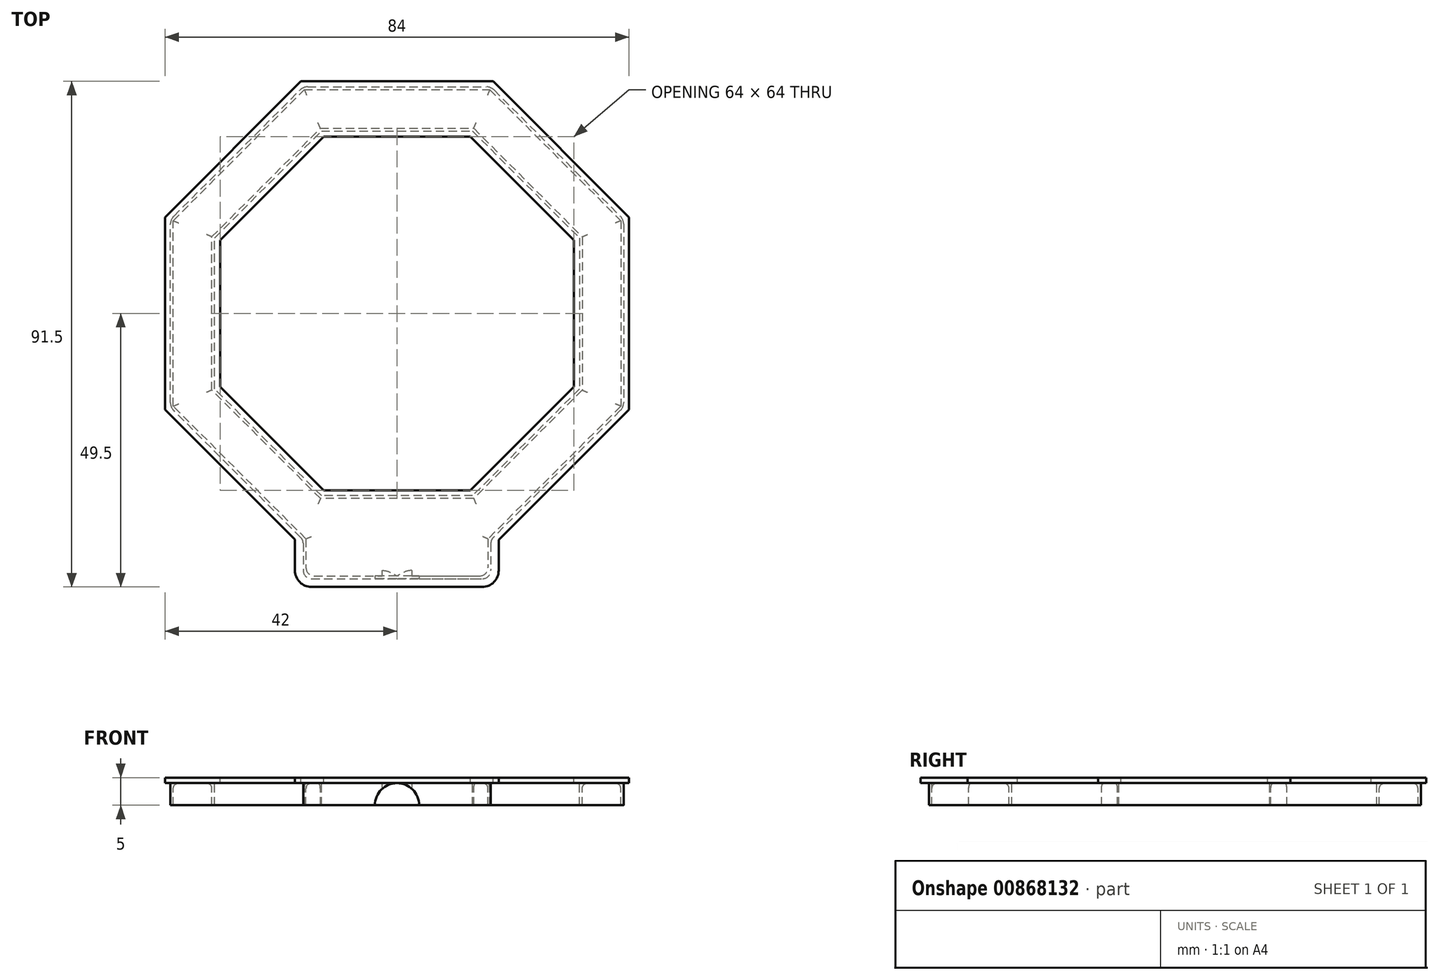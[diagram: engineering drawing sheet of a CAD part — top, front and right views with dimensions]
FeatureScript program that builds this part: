
annotation { "Feature Type Name" : "Feature", "Feature Type Description" : "" }
export const myFeature = defineFeature(function(context is Context, id is Id, definition is map)
    precondition{}
    {
        {
            var Q0;
            Q0=qCreatedBy(makeId("Top.planeOp"),FACE);
            var sketch = newSketch(context, id + "F0", { "sketchPlane" : qUnion([Q0])});
            skCircle(sketch, "E0.cCircle", {"center": v(0, 0) * mm, "radius": 41 * mm, "construction": true});
            skLineSegment(sketch, "E0.0", {"start": v(41, 16.98) * mm, "end": v(41, -16.98) * mm});
            skLineSegment(sketch, "E0.1", {"start": v(41, -16.98) * mm, "end": v(16.98, -41) * mm});
            skLineSegment(sketch, "E0.3", {"start": v(-16.98, -41) * mm, "end": v(-41, -16.98) * mm});
            skLineSegment(sketch, "E0.4", {"start": v(-41, -16.98) * mm, "end": v(-41, 16.98) * mm});
            skLineSegment(sketch, "E0.5", {"start": v(-41, 16.98) * mm, "end": v(-16.98, 41) * mm});
            skLineSegment(sketch, "E0.6", {"start": v(-16.98, 41) * mm, "end": v(16.98, 41) * mm});
            skLineSegment(sketch, "E0.7", {"start": v(16.98, 41) * mm, "end": v(41, 16.98) * mm});
            skPoint(sketch, "E0.0.midPoint", {"position": v(41, 0) * mm});
            skCircle(sketch, "E1.cCircle", {"center": v(0, 0) * mm, "radius": 33 * mm, "construction": true});
            skLineSegment(sketch, "E1.0", {"start": v(-33, 13.67) * mm, "end": v(-13.67, 33) * mm});
            skLineSegment(sketch, "E1.1", {"start": v(-13.67, 33) * mm, "end": v(13.67, 33) * mm});
            skLineSegment(sketch, "E1.2", {"start": v(13.67, 33) * mm, "end": v(33, 13.67) * mm});
            skLineSegment(sketch, "E1.3", {"start": v(33, 13.67) * mm, "end": v(33, -13.67) * mm});
            skLineSegment(sketch, "E1.4", {"start": v(33, -13.67) * mm, "end": v(13.67, -33) * mm});
            skLineSegment(sketch, "E1.5", {"start": v(13.67, -33) * mm, "end": v(-13.67, -33) * mm});
            skLineSegment(sketch, "E1.6", {"start": v(-13.67, -33) * mm, "end": v(-33, -13.67) * mm});
            skLineSegment(sketch, "E1.7", {"start": v(-33, -13.67) * mm, "end": v(-33, 13.67) * mm});
            skPoint(sketch, "E1.0.midPoint", {"position": v(-23.33, 23.33) * mm});
            skLineSegment(sketch, "E2.left", {"start": v(-16.98, -41) * mm, "end": v(-16.98, -48) * mm});
            skCircle(sketch, "E3.cCircle", {"center": v(0, 0) * mm, "radius": 32 * mm, "construction": true});
            skLineSegment(sketch, "E3.0", {"start": v(-13.25, 32) * mm, "end": v(13.25, 32) * mm});
            skLineSegment(sketch, "E3.1", {"start": v(13.25, 32) * mm, "end": v(32, 13.25) * mm});
            skLineSegment(sketch, "E3.2", {"start": v(32, 13.25) * mm, "end": v(32, -13.25) * mm});
            skLineSegment(sketch, "E3.3", {"start": v(32, -13.25) * mm, "end": v(13.25, -32) * mm});
            skLineSegment(sketch, "E3.4", {"start": v(13.25, -32) * mm, "end": v(-13.25, -32) * mm});
            skLineSegment(sketch, "E3.5", {"start": v(-13.25, -32) * mm, "end": v(-32, -13.25) * mm});
            skLineSegment(sketch, "E3.6", {"start": v(-32, -13.25) * mm, "end": v(-32, 13.25) * mm});
            skLineSegment(sketch, "E3.7", {"start": v(-32, 13.25) * mm, "end": v(-13.25, 32) * mm});
            skPoint(sketch, "E3.0.midPoint", {"position": v(0, 32) * mm});
            skCircle(sketch, "E4.cCircle", {"center": v(0, 0) * mm, "radius": 42 * mm, "construction": true});
            skLineSegment(sketch, "E4.0", {"start": v(-42, 17.4) * mm, "end": v(-17.4, 42) * mm});
            skLineSegment(sketch, "E4.1", {"start": v(-17.4, 42) * mm, "end": v(17.4, 42) * mm});
            skLineSegment(sketch, "E4.2", {"start": v(17.4, 42) * mm, "end": v(42, 17.4) * mm});
            skLineSegment(sketch, "E4.3", {"start": v(42, 17.4) * mm, "end": v(42, -17.4) * mm});
            skLineSegment(sketch, "E4.4", {"start": v(42, -17.4) * mm, "end": v(18.4, -41) * mm});
            skLineSegment(sketch, "E4.6", {"start": v(-18.48, -40.91) * mm, "end": v(-42, -17.4) * mm});
            skLineSegment(sketch, "E4.7", {"start": v(-42, -17.4) * mm, "end": v(-42, 17.4) * mm});
            skPoint(sketch, "E4.0.midPoint", {"position": v(-29.7, 29.7) * mm});
            skLineSegment(sketch, "E5", {"start": v(-18.48, -40.91) * mm, "end": v(-18.48, -49.5) * mm});
            skPoint(sketch, "E6.orphan", {"position": v(-17.4, -42) * mm});
            skLineSegment(sketch, "E7", {"start": v(-16.98, -48) * mm, "end": v(16.98, -48) * mm});
            skLineSegment(sketch, "E8", {"start": v(-18.48, -49.5) * mm, "end": v(18.4, -49.5) * mm});
            skLineSegment(sketch, "E9", {"start": v(18.4, -49.5) * mm, "end": v(18.4, -41) * mm});
            skLineSegment(sketch, "E10", {"start": v(16.98, -41) * mm, "end": v(16.98, -48) * mm});
            skLineSegment(sketch, "E11.0", {"start": v(-33.5, 13.88) * mm, "end": v(-13.88, 33.5) * mm});
            skLineSegment(sketch, "E11.1", {"start": v(-33.5, -13.88) * mm, "end": v(-33.5, 13.88) * mm});
            skLineSegment(sketch, "E11.2", {"start": v(-13.88, 33.5) * mm, "end": v(13.88, 33.5) * mm});
            skLineSegment(sketch, "E11.3", {"start": v(-13.88, -33.5) * mm, "end": v(-33.5, -13.88) * mm});
            skLineSegment(sketch, "E11.4", {"start": v(13.88, 33.5) * mm, "end": v(33.5, 13.88) * mm});
            skLineSegment(sketch, "E11.5", {"start": v(33.5, 13.88) * mm, "end": v(33.5, -13.88) * mm});
            skLineSegment(sketch, "E11.6", {"start": v(33.5, -13.88) * mm, "end": v(13.88, -33.5) * mm});
            skLineSegment(sketch, "E11.7", {"start": v(13.88, -33.5) * mm, "end": v(-13.88, -33.5) * mm});
            skLineSegment(sketch, "E12.0", {"start": v(-16.48, -40.8) * mm, "end": v(-16.48, -47.5) * mm});
            skLineSegment(sketch, "E12.1", {"start": v(-16.48, -47.5) * mm, "end": v(16.48, -47.5) * mm});
            skLineSegment(sketch, "E12.2", {"start": v(-16.48, -40.8) * mm, "end": v(-40.5, -16.78) * mm});
            skLineSegment(sketch, "E12.3", {"start": v(16.48, -40.8) * mm, "end": v(16.48, -47.5) * mm});
            skLineSegment(sketch, "E12.4", {"start": v(40.5, -16.78) * mm, "end": v(16.48, -40.8) * mm});
            skLineSegment(sketch, "E12.5", {"start": v(40.5, 16.78) * mm, "end": v(40.5, -16.78) * mm});
            skLineSegment(sketch, "E12.6", {"start": v(-40.5, -16.78) * mm, "end": v(-40.5, 16.78) * mm});
            skLineSegment(sketch, "E12.7", {"start": v(-40.5, 16.78) * mm, "end": v(-16.78, 40.5) * mm});
            skLineSegment(sketch, "E12.8", {"start": v(-16.78, 40.5) * mm, "end": v(16.78, 40.5) * mm});
            skLineSegment(sketch, "E12.9", {"start": v(16.78, 40.5) * mm, "end": v(40.5, 16.78) * mm});
            skSolve(sketch);
        }
        {
            var Q0;
            Q0=makeQuery(id+"F0.imprint","IMPRINT",FACE,{"disambiguationData":[TD([[makeQuery(id+"F0.imprint","IMPRINT",EDGE,{"derivedFrom":sQuery(id+"F0.wireOp",EDGE,"E1.0")}),1.0]])]});
            var Q1;
            Q1=makeQuery(id+"F0.imprint","IMPRINT",FACE,{"disambiguationData":[TD([[makeQuery(id+"F0.imprint","IMPRINT",EDGE,{"derivedFrom":sQuery(id+"F0.wireOp",EDGE,"E0.0")}),-1.0]])]});
            extrude(context, id + "F1", {"entities" : qUnion([Q0, Q1]), "oppositeDirection" : true, "depth" : 5 * mm, "offsetDistance" : 25 * mm});
        }
        {
            var Q0;
            Q0=makeQuery(id+"F0.imprint","IMPRINT",FACE,{"disambiguationData":[TD([[makeQuery(id+"F0.imprint","IMPRINT",EDGE,{"derivedFrom":sQuery(id+"F0.wireOp",EDGE,"E1.0")}),-1.0]])]});
            var Q1;
            Q1=makeQuery(id+"F0.imprint","IMPRINT",FACE,{"disambiguationData":[TD([[makeQuery(id+"F0.imprint","IMPRINT",EDGE,{"derivedFrom":sQuery(id+"F0.wireOp",EDGE,"E11.0")}),1.0]])]});
            var Q2;
            Q2=makeQuery(id+"F0.imprint","IMPRINT",FACE,{"disambiguationData":[TD([[makeQuery(id+"F0.imprint","IMPRINT",EDGE,{"derivedFrom":sQuery(id+"F0.wireOp",EDGE,"E0.0")}),1.0]])]});
            extrude(context, id + "F2", {"entities" : qUnion([Q0, Q1, Q2]), "operationType" : NewBodyOperationType.ADD, "oppositeDirection" : true, "depth" : 1 * mm, "offsetDistance" : 25 * mm});
        }
        {
            var Q0;
            Q0=makeQuery(id+"F1.opExtrude","SWEPT_FACE",FACE,{"disambiguationData":[OSD([sQuery(id+"F0.wireOp",EDGE,"E7")])]});
            var sketch = newSketch(context, id + "F3", { "sketchPlane" : qUnion([Q0])});
            skCircle(sketch, "E13", {"center": v(0, -5) * mm, "radius": 4 * mm});
            skSolve(sketch);
        }
        {
            var Q0;
            {var subQ0=sQuery(id+"F3.wireOp",EDGE,"E13");var subQ1=sQuery(id+"F0.wireOp",EDGE,"E7");var subQ2=makeQuery(id+"F3.imprint","INTERSECT",VERTEX,{"derivedFrom":[makeQuery(id+"F2.opExtrude","CAP_EDGE",EDGE,{"disambiguationData":[OSD([subQ1])],"isStart":false}),subQ0]});Q0=makeQuery(id+"F3.imprint","IMPRINT",FACE,{"disambiguationData":[TD([[makeQuery(id+"F3.imprint","IMPRINT",EDGE,{"disambiguationData":[TD([[subQ2,1.0]])],"derivedFrom":subQ0}),1.0]])]});}
            extrude(context, id + "F4", {"entities" : qUnion([Q0]), "operationType" : NewBodyOperationType.REMOVE, "oppositeDirection" : true, "depth" : 3 * mm, "offsetDistance" : 25 * mm});
        }
        {
            var Q0;
            Q0=makeQuery(id+"F1.opExtrude","SWEPT_EDGE",EDGE,{"disambiguationData":[OSD([sQuery(id+"F0.wireOp",EDGE,"E0.0"),sQuery(id+"F0.wireOp",EDGE,"E0.7")])]});
            var Q1;
            Q1=makeQuery(id+"F1.opExtrude","SWEPT_EDGE",EDGE,{"disambiguationData":[OSD([sQuery(id+"F0.wireOp",EDGE,"E0.0"),sQuery(id+"F0.wireOp",EDGE,"E0.1")])]});
            var Q2;
            Q2=makeQuery(id+"F1.opExtrude","SWEPT_EDGE",EDGE,{"disambiguationData":[OSD([sQuery(id+"F0.wireOp",EDGE,"E0.3"),sQuery(id+"F0.wireOp",EDGE,"E0.4")])]});
            var Q3;
            Q3=makeQuery(id+"F1.opExtrude","SWEPT_EDGE",EDGE,{"disambiguationData":[OSD([sQuery(id+"F0.wireOp",EDGE,"E0.4"),sQuery(id+"F0.wireOp",EDGE,"E0.5")])]});
            var Q4;
            Q4=makeQuery(id+"F1.opExtrude","SWEPT_EDGE",EDGE,{"disambiguationData":[OSD([sQuery(id+"F0.wireOp",EDGE,"E0.5"),sQuery(id+"F0.wireOp",EDGE,"E0.6")])]});
            var Q5;
            Q5=makeQuery(id+"F1.opExtrude","SWEPT_EDGE",EDGE,{"disambiguationData":[OSD([sQuery(id+"F0.wireOp",EDGE,"E0.6"),sQuery(id+"F0.wireOp",EDGE,"E0.7")])]});
            fillet(context, id + "F5", {"entities" : qUnion([Q0, Q1, Q2, Q3, Q4, Q5]), "radius" : 2 * mm, "tangentPropagation" : true, "allowEdgeOverflow" : false});
        }
        {
            var Q0;
            Q0=makeQuery(id+"F1.opExtrude","SWEPT_EDGE",EDGE,{"disambiguationData":[OSD([sQuery(id+"F0.wireOp",EDGE,"E0.1"),sQuery(id+"F0.wireOp",EDGE,"E10")])]});
            var Q1;
            Q1=makeQuery(id+"F1.opExtrude","SWEPT_EDGE",EDGE,{"disambiguationData":[OSD([sQuery(id+"F0.wireOp",EDGE,"E0.3"),sQuery(id+"F0.wireOp",EDGE,"E2.left")])]});
            var Q2;
            Q2=makeQuery(id+"F1.opExtrude","SWEPT_EDGE",EDGE,{"disambiguationData":[OSD([sQuery(id+"F0.wireOp",EDGE,"E7"),sQuery(id+"F0.wireOp",EDGE,"E10")])]});
            var Q3;
            Q3=makeQuery(id+"F1.opExtrude","SWEPT_EDGE",EDGE,{"disambiguationData":[OSD([sQuery(id+"F0.wireOp",EDGE,"E12.0"),sQuery(id+"F0.wireOp",EDGE,"E12.1")])]});
            var Q4;
            Q4=makeQuery(id+"F1.opExtrude","SWEPT_EDGE",EDGE,{"disambiguationData":[OSD([sQuery(id+"F0.wireOp",EDGE,"E12.1"),sQuery(id+"F0.wireOp",EDGE,"E12.3")])]});
            var Q5;
            Q5=makeQuery(id+"F1.opExtrude","SWEPT_EDGE",EDGE,{"disambiguationData":[OSD([sQuery(id+"F0.wireOp",EDGE,"E2.left"),sQuery(id+"F0.wireOp",EDGE,"E7")])]});
            fillet(context, id + "F6", {"entities" : qUnion([Q0, Q1, Q2, Q3, Q4, Q5]), "radius" : 1.5 * mm, "tangentPropagation" : true, "allowEdgeOverflow" : false});
        }
        {
            var Q0;
            Q0=makeQuery(id+"F2.opExtrude","CAP_FACE",FACE,{"disambiguationData":[OSD([sQuery(id+"F0.wireOp",EDGE,"E11.0"),sQuery(id+"F0.wireOp",EDGE,"E11.1"),sQuery(id+"F0.wireOp",EDGE,"E11.2"),sQuery(id+"F0.wireOp",EDGE,"E11.3"),sQuery(id+"F0.wireOp",EDGE,"E11.4"),sQuery(id+"F0.wireOp",EDGE,"E11.5"),sQuery(id+"F0.wireOp",EDGE,"E11.6"),sQuery(id+"F0.wireOp",EDGE,"E11.7"),sQuery(id+"F0.wireOp",EDGE,"E12.0"),sQuery(id+"F0.wireOp",EDGE,"E12.1"),sQuery(id+"F0.wireOp",EDGE,"E12.2"),sQuery(id+"F0.wireOp",EDGE,"E12.3"),sQuery(id+"F0.wireOp",EDGE,"E12.4"),sQuery(id+"F0.wireOp",EDGE,"E12.5"),sQuery(id+"F0.wireOp",EDGE,"E12.6"),sQuery(id+"F0.wireOp",EDGE,"E12.7"),sQuery(id+"F0.wireOp",EDGE,"E12.8"),sQuery(id+"F0.wireOp",EDGE,"E12.9")])],"isStart":false});
            fillet(context, id + "F7", {"entities" : qUnion([Q0]), "radius" : 1 * mm, "tangentPropagation" : true, "allowEdgeOverflow" : false});
        }
        {
            var Q0;
            Q0=makeQuery(id+"F2.opExtrude","SWEPT_EDGE",EDGE,{"disambiguationData":[OSD([sQuery(id+"F0.wireOp",EDGE,"E8"),sQuery(id+"F0.wireOp",EDGE,"E9")])]});
            var Q1;
            Q1=makeQuery(id+"F2.opExtrude","SWEPT_EDGE",EDGE,{"disambiguationData":[OSD([sQuery(id+"F0.wireOp",EDGE,"E5"),sQuery(id+"F0.wireOp",EDGE,"E8")])]});
            fillet(context, id + "F8", {"entities" : qUnion([Q0, Q1]), "radius" : 3 * mm, "tangentPropagation" : true, "allowEdgeOverflow" : false});
        }
    });
